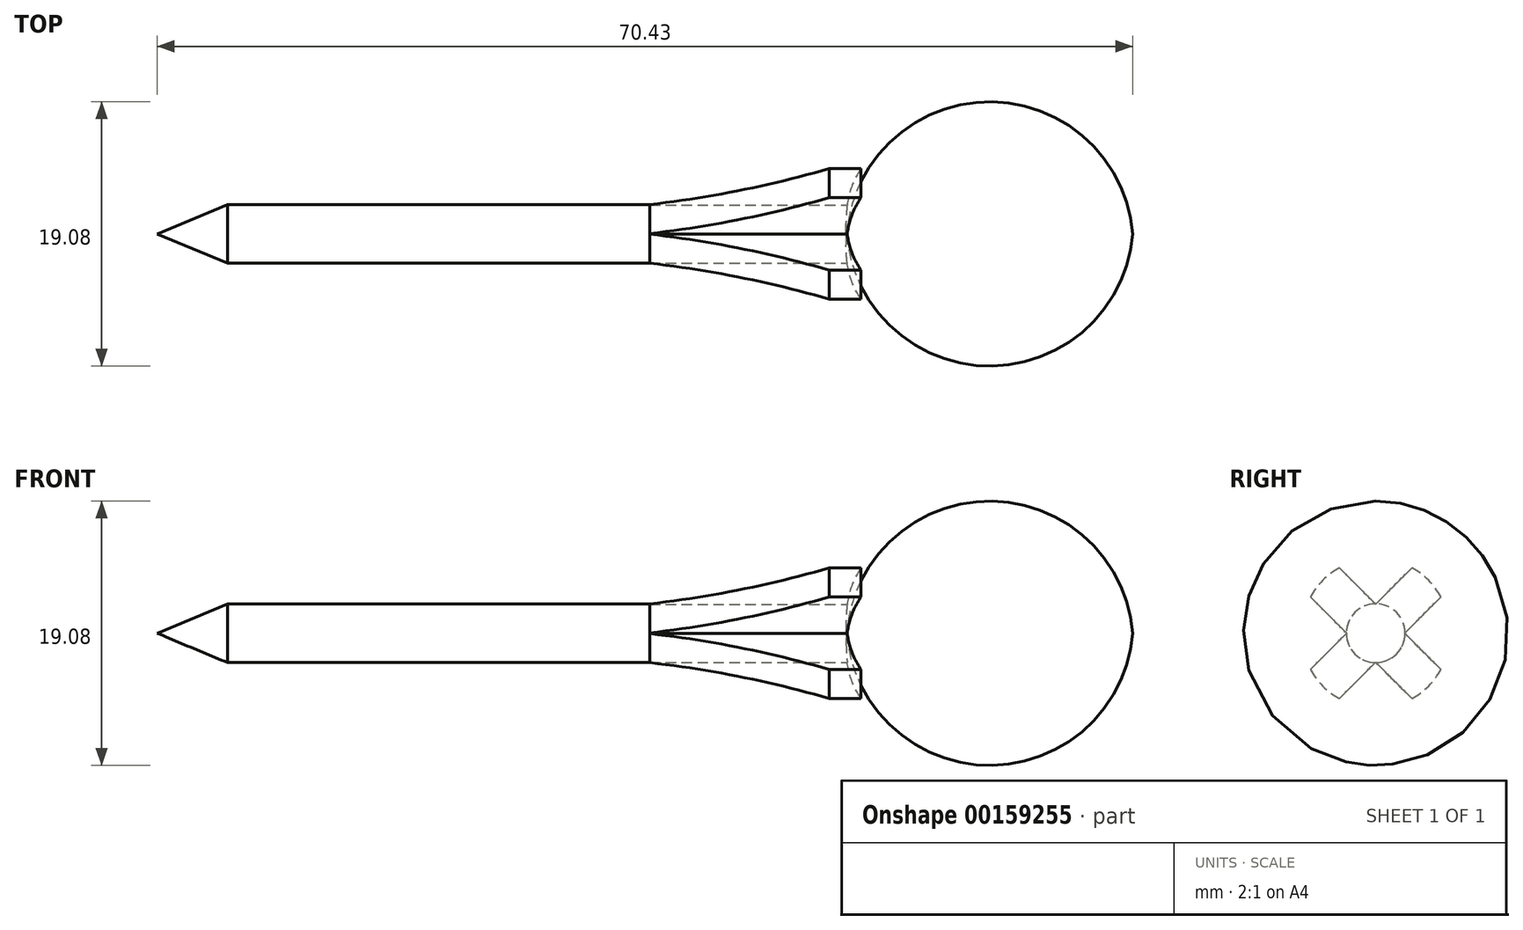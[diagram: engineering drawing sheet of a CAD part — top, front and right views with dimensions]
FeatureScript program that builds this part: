
annotation { "Feature Type Name" : "Feature", "Feature Type Description" : "" }
export const myFeature = defineFeature(function(context is Context, id is Id, definition is map)
    precondition{}
    {
        {
            var Q0;
            Q0=qCreatedBy(makeId("Top.planeOp"),FACE);
            var sketch = newSketch(context, id + "F0", { "sketchPlane" : qUnion([Q0]), "disableImprinting" : false});
            skLineSegment(sketch, "E0", {"start": v(0, 5.4) * mm, "end": v(-2.29, 5.4) * mm});
            skPoint(sketch, "E1", {"position": v(0, 0) * mm});
            skArc(sketch, "E2", {"start": v(-15.24, 2.12) * mm, "mid": v(-8.65, 3.33) * mm, "end": v(-2.29, 5.4) * mm});
            skLineSegment(sketch, "E3", {"start": v(-15.24, 2.12) * mm, "end": v(-45.73, 2.12) * mm});
            skLineSegment(sketch, "E4", {"start": v(-45.73, 2.12) * mm, "end": v(-50.81, 0) * mm});
            skArc(sketch, "E5", {"start": v(0, 5.4) * mm, "mid": v(-0.88, 2.77) * mm, "end": v(-1.03, 0) * mm});
            skLineSegment(sketch, "E6", {"start": v(-1.03, 0) * mm, "end": v(-50.81, 0) * mm});
            skSolve(sketch);
        }
        {
            var Q0;
            Q0=makeQuery(id+"F0.imprint","IMPRINT",FACE,{"disambiguationData":[TD([[makeQuery(id+"F0.imprint","IMPRINT",EDGE,{"derivedFrom":sQuery(id+"F0.wireOp",EDGE,"E0")}),1.0]])]});
            var Q1;
            Q1=sQuery(id+"F0.wireOp",EDGE,"E6");
            revolve(context, id + "F1", {"entities" : qUnion([Q0]), "axis" : qUnion([Q1]), "revolveType" : RevolveType.FULL});
        }
        {
            var Q0;
            Q0=qCreatedBy(makeId("Right.planeOp"),FACE);
            var sketch = newSketch(context, id + "F2", { "sketchPlane" : qUnion([Q0]), "disableImprinting" : false});
            skLineSegment(sketch, "E7", {"start": v(0, 0) * mm, "end": v(-2.1, 0) * mm, "construction": true});
            skLineSegment(sketch, "E8", {"start": v(0, 0) * mm, "end": v(2.1, 0) * mm, "construction": true});
            skLineSegment(sketch, "E9", {"start": v(0, 0) * mm, "end": v(0, -2.1) * mm, "construction": true});
            skLineSegment(sketch, "E10", {"start": v(0, 0) * mm, "end": v(0, 2.1) * mm, "construction": true});
            skLineSegment(sketch, "E11", {"start": v(0, -2.1) * mm, "end": v(-2.1, 0) * mm, "construction": true});
            skLineSegment(sketch, "E12", {"start": v(0, -2.1) * mm, "end": v(3.83, -5.93) * mm});
            skLineSegment(sketch, "E13", {"start": v(2.1, 0) * mm, "end": v(0, -2.1) * mm, "construction": true});
            skLineSegment(sketch, "E14", {"start": v(2.1, 0) * mm, "end": v(0, 2.1) * mm, "construction": true});
            skLineSegment(sketch, "E15", {"start": v(0, 2.1) * mm, "end": v(-2.1, 0) * mm, "construction": true});
            skLineSegment(sketch, "E16", {"start": v(0, -2.1) * mm, "end": v(-3.83, -5.93) * mm});
            skLineSegment(sketch, "E17", {"start": v(-3.83, -5.93) * mm, "end": v(3.83, -5.93) * mm});
            skLineSegment(sketch, "E18", {"start": v(-2.1, 0) * mm, "end": v(-6.42, -4.33) * mm});
            skLineSegment(sketch, "E19", {"start": v(-2.1, 0) * mm, "end": v(-6.42, 4.33) * mm});
            skLineSegment(sketch, "E20", {"start": v(-6.42, 4.33) * mm, "end": v(-6.42, -4.33) * mm});
            skLineSegment(sketch, "E21", {"start": v(2.1, 0) * mm, "end": v(6.06, -3.97) * mm});
            skLineSegment(sketch, "E22", {"start": v(2.1, 0) * mm, "end": v(6.06, 3.97) * mm});
            skLineSegment(sketch, "E23", {"start": v(6.06, 3.97) * mm, "end": v(6.06, -3.97) * mm});
            skLineSegment(sketch, "E24", {"start": v(0, 2.1) * mm, "end": v(-4.49, 6.58) * mm});
            skLineSegment(sketch, "E25", {"start": v(0, 2.1) * mm, "end": v(4.49, 6.58) * mm});
            skLineSegment(sketch, "E26", {"start": v(4.49, 6.58) * mm, "end": v(-4.49, 6.58) * mm});
            skSolve(sketch);
        }
        {
            var Q0;
            Q0 = qSketchRegion(id + "F2", true);
            extrude(context, id + "F3", {"entities" : qUnion([Q0]), "operationType" : NewBodyOperationType.REMOVE, "oppositeDirection" : true, "depth" : 15.24 * mm});
        }
    });
